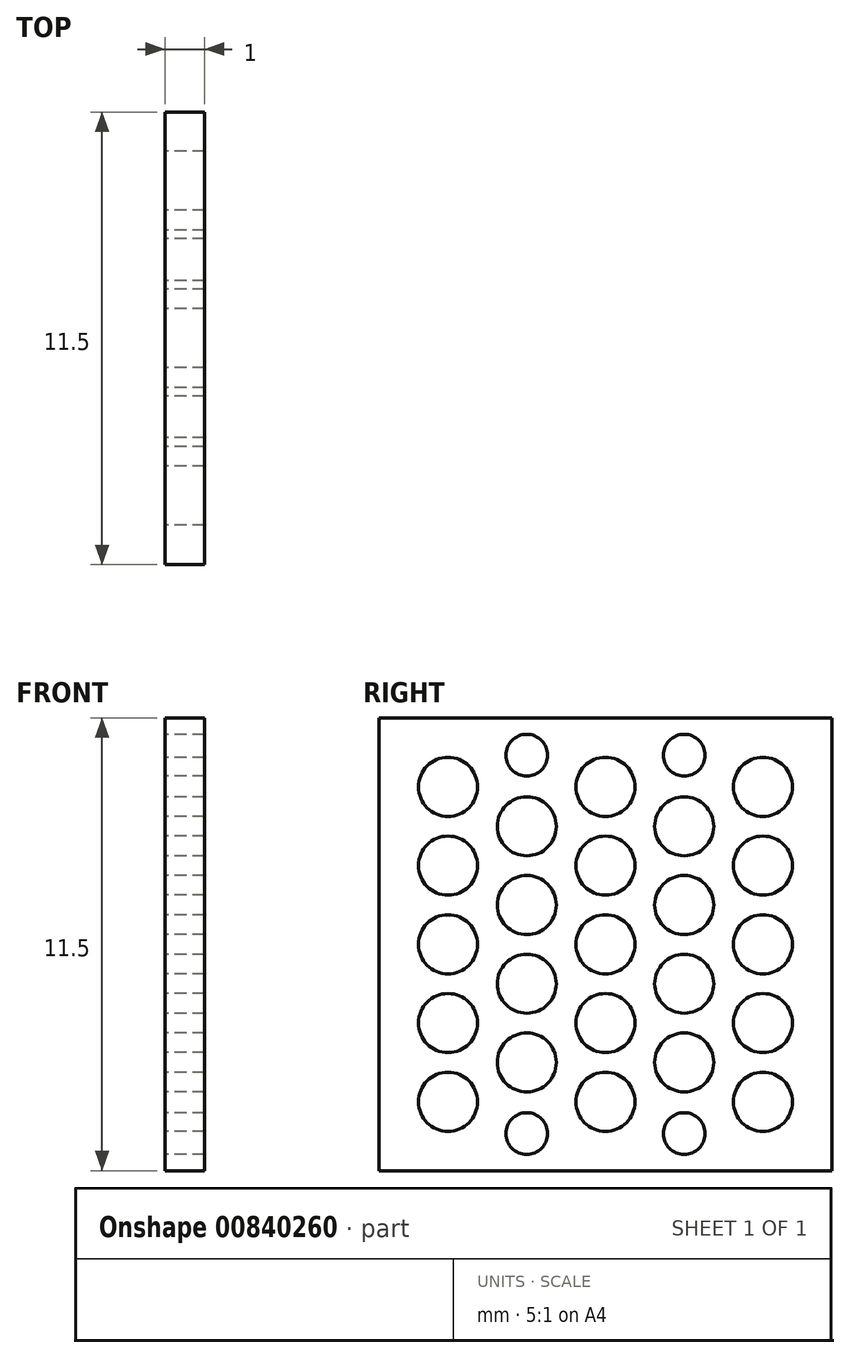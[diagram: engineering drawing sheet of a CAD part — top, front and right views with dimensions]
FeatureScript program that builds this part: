
annotation { "Feature Type Name" : "Feature", "Feature Type Description" : "" }
export const myFeature = defineFeature(function(context is Context, id is Id, definition is map)
    precondition{}
    {
        {
            var Q0;
            Q0=qCreatedBy(makeId("Right.planeOp"),FACE);
            var sketch = newSketch(context, id + "F0", { "sketchPlane" : qUnion([Q0])});
            skLineSegment(sketch, "E0.bottom", {"start": v(0, 0) * mm, "end": v(8.38, 0) * mm});
            skLineSegment(sketch, "E0.top", {"start": v(0, -11.5) * mm, "end": v(11.5, -11.5) * mm});
            skLineSegment(sketch, "E0.left", {"start": v(0, 0) * mm, "end": v(0, -11.5) * mm});
            skLineSegment(sketch, "E1", {"start": v(11.5, 0) * mm, "end": v(11.5, -11.5) * mm});
            skLineSegment(sketch, "E2", {"start": v(10.38, 0) * mm, "end": v(10.38, 10) * mm});
            skLineSegment(sketch, "E3", {"start": v(10.38, 10) * mm, "end": v(8.38, 10) * mm});
            skLineSegment(sketch, "E4", {"start": v(8.38, 10) * mm, "end": v(8.38, 0) * mm});
            skLineSegment(sketch, "E5.trimOffspring", {"start": v(10.38, 0) * mm, "end": v(11.5, 0) * mm});
            skCircle(sketch, "E6", {"center": v(1.75, -5.75) * mm, "radius": 0.75 * mm});
            skCircle(sketch, "E7.MirrorC", {"center": v(1.75, -1.75) * mm, "radius": 0.75 * mm});
            skCircle(sketch, "E8.MirrorC", {"center": v(1.75, -3.75) * mm, "radius": 0.75 * mm});
            skCircle(sketch, "E9.MirrorC", {"center": v(1.75, -9.75) * mm, "radius": 0.75 * mm});
            skCircle(sketch, "E10.MirrorC", {"center": v(1.75, -7.75) * mm, "radius": 0.75 * mm});
            skCircle(sketch, "E11", {"center": v(3.75, -2.75) * mm, "radius": 0.75 * mm});
            skCircle(sketch, "E12", {"center": v(3.75, -10.56) * mm, "radius": 0.53 * mm});
            skCircle(sketch, "E13.MirrorC", {"center": v(5.75, -1.75) * mm, "radius": 0.75 * mm});
            skCircle(sketch, "E14.MirrorC", {"center": v(5.75, -3.75) * mm, "radius": 0.75 * mm});
            skCircle(sketch, "E15.MirrorC", {"center": v(5.75, -5.75) * mm, "radius": 0.75 * mm});
            skCircle(sketch, "E16.MirrorC", {"center": v(5.75, -7.75) * mm, "radius": 0.75 * mm});
            skCircle(sketch, "E17.MirrorC", {"center": v(5.75, -9.75) * mm, "radius": 0.75 * mm});
            skCircle(sketch, "E18.MirrorC", {"center": v(7.75, -2.75) * mm, "radius": 0.75 * mm});
            skCircle(sketch, "E19.MirrorC", {"center": v(9.75, -1.75) * mm, "radius": 0.75 * mm});
            skCircle(sketch, "E20.MirrorC", {"center": v(9.75, -3.75) * mm, "radius": 0.75 * mm});
            skCircle(sketch, "E21.MirrorC", {"center": v(9.75, -5.75) * mm, "radius": 0.75 * mm});
            skCircle(sketch, "E22.MirrorC", {"center": v(9.75, -7.75) * mm, "radius": 0.75 * mm});
            skCircle(sketch, "E23.MirrorC", {"center": v(9.75, -9.75) * mm, "radius": 0.75 * mm});
            skCircle(sketch, "E24", {"center": v(7.75, -10.56) * mm, "radius": 0.53 * mm});
            skCircle(sketch, "E25", {"center": v(3.75, -0.94) * mm, "radius": 0.53 * mm});
            skCircle(sketch, "E26", {"center": v(7.75, -0.94) * mm, "radius": 0.53 * mm});
            skCircle(sketch, "E27", {"center": v(3.75, -4.75) * mm, "radius": 0.75 * mm});
            skCircle(sketch, "E28", {"center": v(3.75, -6.75) * mm, "radius": 0.75 * mm});
            skCircle(sketch, "E29", {"center": v(3.75, -8.75) * mm, "radius": 0.75 * mm});
            skCircle(sketch, "E30.MirrorC", {"center": v(7.75, -4.75) * mm, "radius": 0.75 * mm});
            skCircle(sketch, "E31.MirrorC", {"center": v(7.75, -6.75) * mm, "radius": 0.75 * mm});
            skCircle(sketch, "E32.MirrorC", {"center": v(7.75, -8.75) * mm, "radius": 0.75 * mm});
            skLineSegment(sketch, "E33", {"start": v(8.38, 0) * mm, "end": v(10.38, 0) * mm});
            skSolve(sketch);
        }
        {
            var Q0;
            Q0=makeQuery(id+"F0.imprint","IMPRINT",FACE,{"disambiguationData":[TD([[makeQuery(id+"F0.imprint","IMPRINT",EDGE,{"derivedFrom":sQuery(id+"F0.wireOp",EDGE,"E0.bottom")}),-1.0]])]});
            var Q1;
            Q1=makeQuery(id+"F0.imprint","IMPRINT",FACE,{"disambiguationData":[TD([[makeQuery(id+"F0.imprint","IMPRINT",EDGE,{"derivedFrom":sQuery(id+"F0.wireOp",EDGE,"r65wuaeR-pUGk-UfhY-v5oq-7bkjaNJfQmKm.bottom")}),-1.0]])]});
            var Q2;
            Q2=makeQuery(id+"F0.imprint","IMPRINT",FACE,{"disambiguationData":[TD([[makeQuery(id+"F0.imprint","IMPRINT",EDGE,{"derivedFrom":sQuery(id+"F0.wireOp",EDGE,"n5EaUuf3-CoM6-EQkv-XzT1-ydr3onYee1LO.bottom")}),1.0]])]});
            var Q3;
            Q3=makeQuery(id+"F0.imprint","IMPRINT",FACE,{"disambiguationData":[TD([[makeQuery(id+"F0.imprint","IMPRINT",EDGE,{"derivedFrom":sQuery(id+"F0.wireOp",EDGE,"2NUbogVr-x7fL-9LVX-WR3f-6RiyyzUn8nbi.bottom")}),-1.0]])]});
            extrude(context, id + "F1", {"entities" : qUnion([Q0, Q1, Q2, Q3]), "depth" : 1 * mm, "offsetDistance" : 25 * mm});
        }
    });
